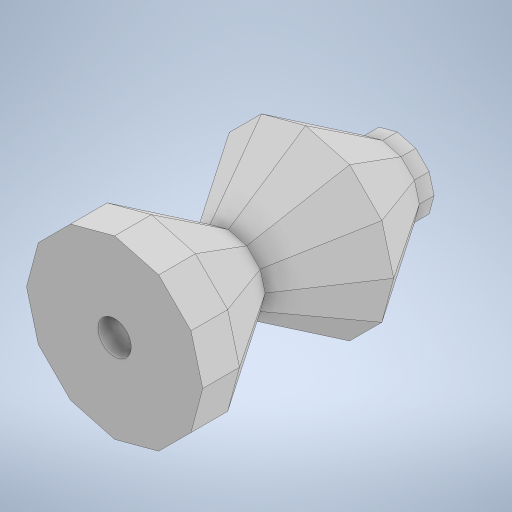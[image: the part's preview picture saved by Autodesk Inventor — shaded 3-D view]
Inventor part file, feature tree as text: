
AUTODESK INVENTOR PART (.ipt)
format: ipt  version: 2023 (Build 270158000, 158)  size: 351,744 bytes
history: native  units: in
note: dims shown in document units (in); Inventor stores cm internally (conversion verified against a paired STEP export)
features: sketch x6, extrude x4, projected_geometry x3, other x2, mirror x2, loft x1, shell x1
ambient origin geometry x8: Origin, YZ Plane, XZ Plane, XY Plane, X Axis, Y Axis, Z Axis, Center Point
bodies: Body1 (feature_tree)
feature tree (19):
  other  "솔리드1"
  sketch  "스케치1"
  other  "작업 평면1"
  loft  "로프트1"
  mirror  "미러1"
  mirror  "미러2"
  extrude  "돌출1"  Depth=0.4134in
  shell  "쉘1"  Thickness=0.3937in
  extrude  "돌출2"  TaperAngle=0.0deg  [1 undecoded]
  extrude  "돌출3"  TaperAngle=0.0deg  [1 undecoded]
  extrude  "돌출4"  Depth=0.0787in TaperAngle=0.0deg
  sketch  "스케치2"
  sketch  "스케치3"
  projected_geometry  "투영된 루프1"
  sketch  "스케치4"
  projected_geometry  "투영된 루프2"
  sketch  "스케치5"
  sketch  "스케치6"
  projected_geometry  "투영된 루프3"
note: 2 required parameter values undecoded (feature->parameter linkage not recoverable at this tier; creation-order binding heuristic only, values carry confidence <= 0.55)
